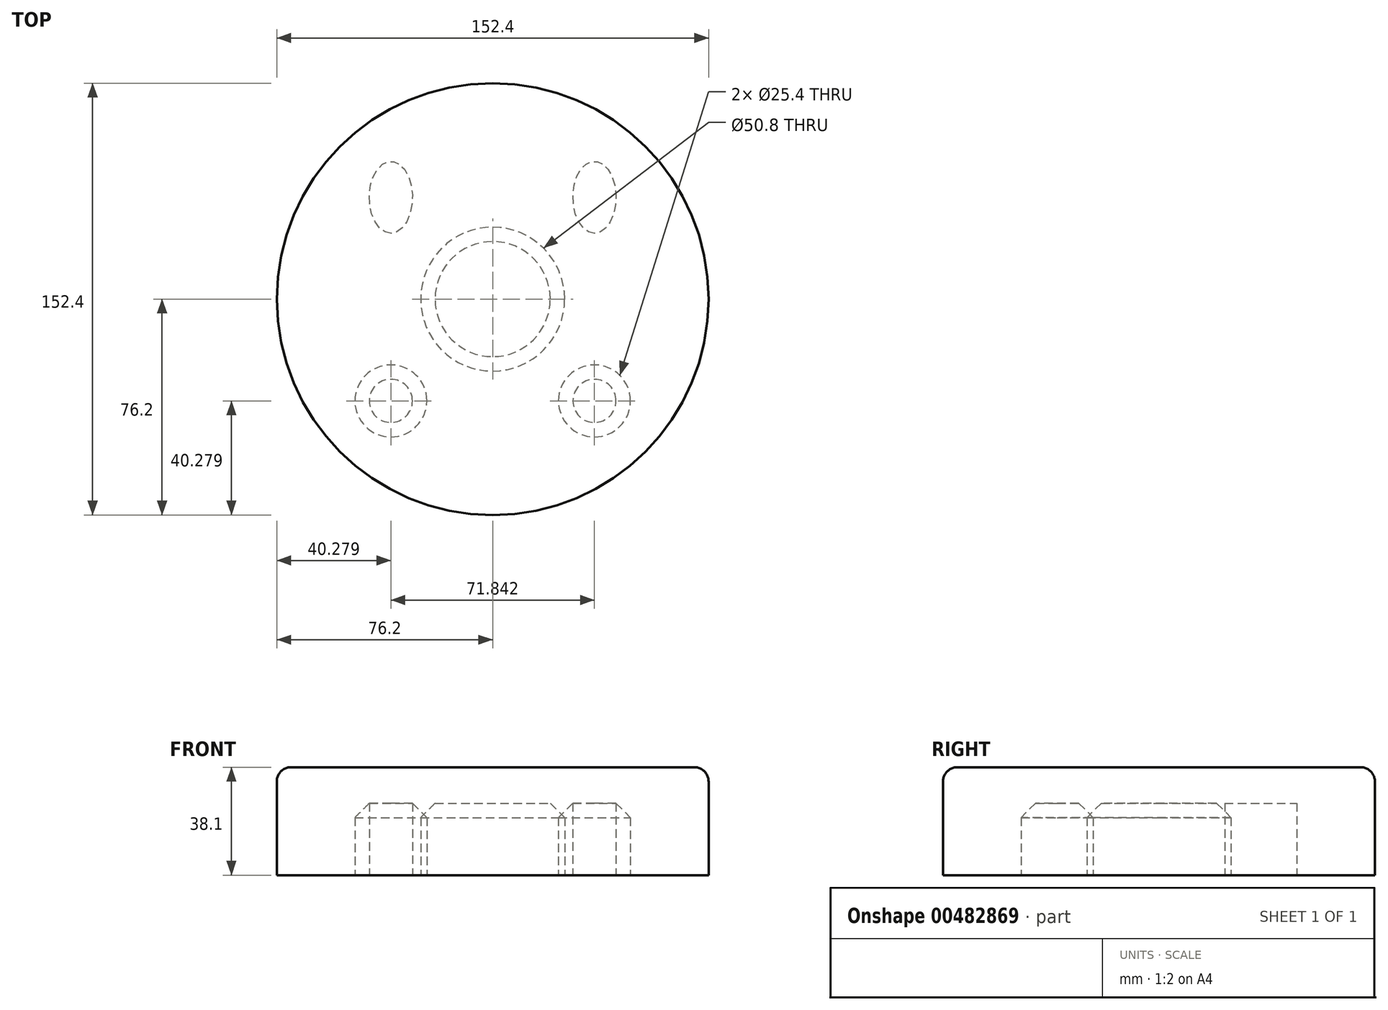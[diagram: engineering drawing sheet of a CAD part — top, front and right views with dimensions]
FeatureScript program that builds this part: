
annotation { "Feature Type Name" : "Feature", "Feature Type Description" : "" }
export const myFeature = defineFeature(function(context is Context, id is Id, definition is map)
    precondition{}
    {
        {
            var Q0;
            Q0=qCreatedBy(makeId("Top.planeOp"),FACE);
            var sketch = newSketch(context, id + "F0", { "sketchPlane" : qUnion([Q0])});
            skCircle(sketch, "E0", {"center": v(0, 0) * mm, "radius": 76.2 * mm});
            skCircle(sketch, "E1", {"center": v(0, 0) * mm, "radius": 31.75 * mm});
            skLineSegment(sketch, "E2", {"start": v(0, 0) * mm, "end": v(-35.92, -35.92) * mm, "construction": true});
            skLineSegment(sketch, "E3", {"start": v(0, 0) * mm, "end": v(35.92, -35.92) * mm, "construction": true});
            skLineSegment(sketch, "E4", {"start": v(0, 0) * mm, "end": v(35.92, 35.92) * mm, "construction": true});
            skLineSegment(sketch, "E5", {"start": v(0, 0) * mm, "end": v(-35.92, 35.92) * mm, "construction": true});
            skEllipse(sketch, "E6", {"center": v(-35.92, -35.92) * mm, "majorRadius": 12.7 * mm, "minorRadius": 7.62 * mm, "majorAxis": v(0, -1)});
            skEllipse(sketch, "E7", {"center": v(35.92, -35.92) * mm, "majorRadius": 12.7 * mm, "minorRadius": 7.62 * mm, "majorAxis": v(0, -1)});
            skCircle(sketch, "E8", {"center": v(-35.92, 35.92) * mm, "radius": 12.7 * mm});
            skCircle(sketch, "E9", {"center": v(35.92, 35.92) * mm, "radius": 12.7 * mm});
            skSolve(sketch);
        }
        {
            var Q0;
            Q0=makeQuery(id+"F0.imprint","IMPRINT",FACE,{"disambiguationData":[TD([[makeQuery(id+"F0.imprint","IMPRINT",EDGE,{"derivedFrom":sQuery(id+"F0.wireOp",EDGE,"E0")}),1.0]])]});
            var Q1;
            Q1=makeQuery(id+"F0.imprint","IMPRINT",FACE,{"disambiguationData":[TD([[makeQuery(id+"F0.imprint","IMPRINT",EDGE,{"derivedFrom":sQuery(id+"F0.wireOp",EDGE,"E8")}),1.0]])]});
            var Q2;
            Q2=makeQuery(id+"F0.imprint","IMPRINT",FACE,{"disambiguationData":[TD([[makeQuery(id+"F0.imprint","IMPRINT",EDGE,{"derivedFrom":sQuery(id+"F0.wireOp",EDGE,"E1")}),1.0]])]});
            var Q3;
            Q3=makeQuery(id+"F0.imprint","IMPRINT",FACE,{"disambiguationData":[TD([[makeQuery(id+"F0.imprint","IMPRINT",EDGE,{"derivedFrom":sQuery(id+"F0.wireOp",EDGE,"E9")}),1.0]])]});
            var Q4;
            Q4=makeQuery(id+"F0.imprint","IMPRINT",FACE,{"disambiguationData":[TD([[makeQuery(id+"F0.imprint","IMPRINT",EDGE,{"derivedFrom":sQuery(id+"F0.wireOp",EDGE,"E7")}),1.0]])]});
            var Q5;
            Q5=makeQuery(id+"F0.imprint","IMPRINT",FACE,{"disambiguationData":[TD([[makeQuery(id+"F0.imprint","IMPRINT",EDGE,{"derivedFrom":sQuery(id+"F0.wireOp",EDGE,"E6")}),1.0]])]});
            extrude(context, id + "F1", {"entities" : qUnion([Q0, Q1, Q2, Q3, Q4, Q5]), "depth" : 38.1 * mm});
        }
        {
            var Q0;
            Q0=makeQuery(id+"F1.opExtrude","CAP_FACE",FACE,{"disambiguationData":[OSD([sQuery(id+"F0.wireOp",EDGE,"E0")])],"isStart":true});
            var sketch = newSketch(context, id + "F2", { "sketchPlane" : qUnion([Q0])});
            skLineSegment(sketch, "E10", {"start": v(0, 0) * mm, "end": v(-35.92, -35.92) * mm, "construction": true});
            skLineSegment(sketch, "E11", {"start": v(0, 0) * mm, "end": v(-35.92, 35.92) * mm, "construction": true});
            skLineSegment(sketch, "E12", {"start": v(0, 0) * mm, "end": v(35.92, 35.92) * mm, "construction": true});
            skLineSegment(sketch, "E13", {"start": v(0, 0) * mm, "end": v(35.92, -35.92) * mm, "construction": true});
            skCircle(sketch, "E14", {"center": v(0, 0) * mm, "radius": 25.4 * mm});
            skCircle(sketch, "E15", {"center": v(35.92, 35.92) * mm, "radius": 12.7 * mm});
            skCircle(sketch, "E16", {"center": v(-35.92, 35.92) * mm, "radius": 12.7 * mm});
            skEllipse(sketch, "E17", {"center": v(-35.92, -35.92) * mm, "majorRadius": 12.7 * mm, "minorRadius": 7.62 * mm, "majorAxis": v(0, 1)});
            skEllipse(sketch, "E18", {"center": v(35.92, -35.92) * mm, "majorRadius": 12.7 * mm, "minorRadius": 7.62 * mm, "majorAxis": v(0, 1)});
            skSolve(sketch);
        }
        {
            var Q0;
            Q0 = qSketchRegion(id + "F2", true);
            extrude(context, id + "F3", {"entities" : qUnion([Q0]), "operationType" : NewBodyOperationType.REMOVE, "oppositeDirection" : true, "depth" : 25.4 * mm});
        }
        {
            var Q0;
            Q0=makeQuery(id+"F1.opExtrude","CAP_EDGE",EDGE,{"disambiguationData":[OSD([sQuery(id+"F0.wireOp",EDGE,"E0")])],"isStart":false});
            fillet(context, id + "F4", {"entities" : qUnion([Q0]), "radius" : 5.08 * mm, "tangentPropagation" : true, "allowEdgeOverflow" : false});
        }
        {
            var Q0;
            Q0=makeQuery(id+"F3.boolean.opBoolean","COPY",EDGE,{"derivedFrom":makeQuery(id+"F3.opExtrude","CAP_EDGE",EDGE,{"disambiguationData":[OSD([sQuery(id+"F2.wireOp",EDGE,"E14")])],"isStart":false})});
            var Q1;
            Q1=makeQuery(id+"F3.boolean.opBoolean","COPY",EDGE,{"derivedFrom":makeQuery(id+"F3.opExtrude","CAP_EDGE",EDGE,{"disambiguationData":[OSD([sQuery(id+"F2.wireOp",EDGE,"E15")])],"isStart":false})});
            chamfer(context, id + "F5", {"entities" : qUnion([Q0, Q1]), "width" : 5.08 * mm, "tangentPropagation" : true});
        }
        {
            var Q0;
            Q0=makeQuery(id+"F3.boolean.opBoolean","COPY",EDGE,{"derivedFrom":makeQuery(id+"F3.opExtrude","CAP_EDGE",EDGE,{"disambiguationData":[OSD([sQuery(id+"F2.wireOp",EDGE,"E16")])],"isStart":false})});
            chamfer(context, id + "F6", {"entities" : qUnion([Q0]), "width" : 5.08 * mm, "tangentPropagation" : true});
        }
    });
